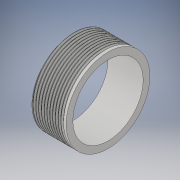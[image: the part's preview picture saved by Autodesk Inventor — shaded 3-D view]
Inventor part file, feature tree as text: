
AUTODESK INVENTOR PART (.ipt)
format: ipt  version: 2019 (Build 230136000, 136)  size: 630,784 bytes
history: native  units: mm
features: sketch x2, extrude x1, helix x1
ambient origin geometry x8: Origin, YZ Plane, XZ Plane, XY Plane, X Axis, Y Axis, Z Axis, Center Point
bodies: Body1 (feature_tree)
feature tree (4):
  extrude  "Extrusion2"  Depth=20.0mm
  helix  "Coil1"  [1 undecoded]
  sketch  "Sketch2"  dims[d0=23.8125mm d3=20.0mm d4=10.0mm d5=0.0mm]
  sketch  "Sketch3"  dims[d6=60.0deg d7=0.79375mm d8=0.694531mm d9=0.198437mm d10=60.0deg d11=0.79375mm d12=0.79375mm d13=10.0mm d14=10.0mm d15=0.0mm d16=90.0deg d17=90.0deg d18=0.0mm d19=0.0mm]
note: 1 required parameter value undecoded (feature->parameter linkage not recoverable at this tier; creation-order binding heuristic only, values carry confidence <= 0.55)
